FCSTD DOCUMENT  (FreeCAD 0.18.4R)
Label: Abanico
License: All rights reserved
LicenseURL: http://en.wikipedia.org/wiki/All_rights_reserved
objects: Part::Part2DObjectPython×70, App::DocumentObjectGroup×1
note: 70 computed .brp shape members not serialized (recipe doc carries the construction recipe); baked Part::Feature solids carry a one-line shape summary decoded from their .brp

FEATURE [Part::Part2DObjectPython] Line  # Draft 2D object (typed FeaturePython)
  ChamferSize = 0
  Closed = true
  End = (47,0,0)
  FilletRadius = 0
  Length = 47
  MakeFace = false
  Points = (2) [(0,0,0),(47,0,0)]
  Start = (0,0,0)
  Subdivisions = 0
FEATURE [Part::Part2DObjectPython] Line001  # Draft 2D object (typed FeaturePython)
  ChamferSize = 0
  Closed = true
  End = (47,7.52818,0)
  FilletRadius = 0
  Length = 15.0564
  MakeFace = false
  Placement = pos=(47,-7.52818,0) rot=(0,0,1;0rad)
  Points = (2) [(0,0,0),(0,15.0564,0)]
  Start = (47,-7.52818,0)
  Subdivisions = 0
FEATURE [Part::Part2DObjectPython] Wire  # Draft 2D object (typed FeaturePython)
  ChamferSize = 0
  Closed = true
  End = (21.85,-0.95,0)
  FilletRadius = 0
  Length = 11.2
  MakeFace = false
  Placement = pos=(21.85,0.95,0) rot=(0,0,1;0rad)
  Points = (4) [(0,0,0),(-3.7,0,0),(-3.7,-1.9,0),(0,-1.9,0)]
  Start = (21.85,0.95,0)
  Subdivisions = 0
FEATURE [Part::Part2DObjectPython] Line002  # Draft 2D object (typed FeaturePython)
  ChamferSize = 0
  Closed = true
  End = (34.0926,32.3527,0)
  FilletRadius = 0
  Length = 47
  MakeFace = false
  Points = (2) [(0,0,0),(34.0926,32.3527,0)]
  Start = (0,0,0)
  Subdivisions = 0
FEATURE [Part::Part2DObjectPython] Line003  # Draft 2D object (typed FeaturePython)
  ChamferSize = 0
  Closed = true
  End = (28.9105,37.8134,0)
  FilletRadius = 0
  Length = 15.0564
  MakeFace = false
  Placement = pos=(39.2747,26.8919,0) rot=(0,0,1;0rad)
  Points = (2) [(0,0,0),(-10.3641,10.9215,0)]
  Start = (39.2747,26.8919,0)
  Subdivisions = 0
FEATURE [Part::Part2DObjectPython] Wire001  # Draft 2D object (typed FeaturePython)
  ChamferSize = 0
  Closed = true
  End = (16.5034,14.3514,0)
  FilletRadius = 0
  Length = 11.2
  MakeFace = false
  Placement = pos=(15.1955,15.7297,0) rot=(0,0,1;0rad)
  Points = (4) [(0,0,0),(-2.68389,-2.54691,0),(-1.37601,-3.92512,0),(1.30787,-1.37821,0)]
  Start = (15.1955,15.7297,0)
  Subdivisions = 0
FEATURE [Part::Part2DObjectPython] Circle  # Draft 2D object (typed FeaturePython)
  FirstAngle = 0
  LastAngle = 0
  MakeFace = false
  Placement = pos=(23.0803,30.1878,0) rot=(0,0,1;0rad)
  Radius = 1.6
FEATURE [Part::Part2DObjectPython] Line004  # Draft 2D object (typed FeaturePython)
  ChamferSize = 0
  Closed = true
  End = (22.2821,41.3824,0)
  FilletRadius = 0
  Length = 47
  MakeFace = false
  Points = (2) [(0,0,0),(22.2821,41.3824,0)]
  Start = (0,0,0)
  Subdivisions = 0
FEATURE [Part::Part2DObjectPython] Line005  # Draft 2D object (typed FeaturePython)
  ChamferSize = 0
  Closed = true
  End = (15.6538,44.9515,0)
  FilletRadius = 0
  Length = 15.0564
  MakeFace = false
  Placement = pos=(28.9105,37.8134,0) rot=(0,0,1;0rad)
  Points = (2) [(0,0,0),(-13.2568,7.13804,0)]
  Start = (28.9105,37.8134,0)
  Subdivisions = 0
FEATURE [Part::Part2DObjectPython] Wire002  # Draft 2D object (typed FeaturePython)
  ChamferSize = 0
  Closed = true
  End = (11.1953,18.788,0)
  FilletRadius = 0
  Length = 11.2
  MakeFace = false
  Placement = pos=(9.52237,19.6888,0) rot=(0,0,1;0rad)
  Points = (4) [(0,0,0),(-1.75413,-3.25777,0),(-0.0812194,-4.15853,0),(1.67291,-0.900768,0)]
  Start = (9.52237,19.6888,0)
  Subdivisions = 0
FEATURE [Part::Part2DObjectPython] Circle001  # Draft 2D object (typed FeaturePython)
  FirstAngle = 0
  LastAngle = 0
  MakeFace = false
  Placement = pos=(12.4969,35.8863,0) rot=(0,0,1;0rad)
  Radius = 1.6
FEATURE [Part::Part2DObjectPython] Line006  # Draft 2D object (typed FeaturePython)
  ChamferSize = 0
  Closed = true
  End = (8.24224,46.2716,0)
  FilletRadius = 0
  Length = 47
  MakeFace = false
  Points = (2) [(0,0,0),(8.24224,46.2716,0)]
  Start = (0,0,0)
  Subdivisions = 0
FEATURE [Part::Part2DObjectPython] Line007  # Draft 2D object (typed FeaturePython)
  ChamferSize = 0
  Closed = true
  End = (0.830719,47.5918,0)
  FilletRadius = 0
  Length = 15.0564
  MakeFace = false
  Placement = pos=(15.6538,44.9515,0) rot=(0,0,1;0rad)
  Points = (2) [(0,0,0),(-14.823,2.64038,0)]
  Start = (15.6538,44.9515,0)
  Subdivisions = 0
FEATURE [Part::Part2DObjectPython] Wire003  # Draft 2D object (typed FeaturePython)
  ChamferSize = 0
  Closed = true
  End = (4.76704,21.3448,0)
  FilletRadius = 0
  Length = 11.2
  MakeFace = false
  Placement = pos=(2.89648,21.678,0) rot=(0,0,1;0rad)
  Points = (4) [(0,0,0),(-0.648857,-3.64266,0),(1.2217,-3.97586,0),(1.87056,-0.333197,0)]
  Start = (2.89648,21.678,0)
  Subdivisions = 0
FEATURE [Part::Part2DObjectPython] Circle002  # Draft 2D object (typed FeaturePython)
  FirstAngle = 0
  LastAngle = 0
  MakeFace = false
  Placement = pos=(0.663191,37.9942,0) rot=(0,0,1;0rad)
  Radius = 1.6
FEATURE [Part::Part2DObjectPython] Line008  # Draft 2D object (typed FeaturePython)
  ChamferSize = 0
  Closed = true
  End = (-6.62236,46.5311,0)
  FilletRadius = 0
  Length = 47
  MakeFace = false
  Points = (2) [(0,0,0),(-6.62236,46.5311,0)]
  Start = (0,0,0)
  Subdivisions = 0
FEATURE [Part::Part2DObjectPython] Line009  # Draft 2D object (typed FeaturePython)
  ChamferSize = 0
  Closed = true
  End = (-14.0754,45.4704,0)
  FilletRadius = 0
  Length = 15.0564
  MakeFace = false
  Placement = pos=(0.830719,47.5918,0) rot=(0,0,1;0rad)
  Points = (2) [(0,0,0),(-14.9062,-2.12146,0)]
  Start = (0.830719,47.5918,0)
  Subdivisions = 0
FEATURE [Part::Part2DObjectPython] Wire004  # Draft 2D object (typed FeaturePython)
  ChamferSize = 0
  Closed = true
  End = (-2.13817,21.7659,0)
  FilletRadius = 0
  Length = 11.2
  MakeFace = false
  Placement = pos=(-4.01921,21.4982,0) rot=(0,0,1;0rad)
  Points = (4) [(0,0,0),(0.521335,-3.66309,0),(2.40238,-3.39538,0),(1.88104,0.267712,0)]
  Start = (-4.01921,21.4982,0)
  Subdivisions = 0
FEATURE [Part::Part2DObjectPython] Circle003  # Draft 2D object (typed FeaturePython)
  FirstAngle = 0
  LastAngle = 0
  MakeFace = false
  Placement = pos=(-11.2369,36.3006,0) rot=(0,0,1;0rad)
  Radius = 1.6
FEATURE [Part::Part2DObjectPython] Line010  # Draft 2D object (typed FeaturePython)
  ChamferSize = 0
  Closed = true
  End = (-20.8243,42.1349,0)
  FilletRadius = 0
  Length = 47
  MakeFace = false
  Points = (2) [(0,0,0),(-20.8243,42.1349,0)]
  Start = (0,0,0)
  Subdivisions = 0
FEATURE [Part::Part2DObjectPython] Line011  # Draft 2D object (typed FeaturePython)
  ChamferSize = 0
  Closed = true
  End = (-27.5733,38.7993,0)
  FilletRadius = 0
  Length = 15.0564
  MakeFace = false
  Placement = pos=(-14.0754,45.4704,0) rot=(0,0,1;0rad)
  Points = (2) [(0,0,0),(-13.4978,-6.67104,0)]
  Start = (-14.0754,45.4704,0)
  Subdivisions = 0
FEATURE [Part::Part2DObjectPython] Wire005  # Draft 2D object (typed FeaturePython)
  ChamferSize = 0
  Closed = true
  End = (-8.82944,20.0091,0)
  FilletRadius = 0
  Length = 11.2
  MakeFace = false
  Placement = pos=(-10.5328,19.1673,0) rot=(0,0,1;0rad)
  Points = (4) [(0,0,0),(1.63936,-3.317,0),(3.34269,-2.47516,0),(1.70332,0.841835,0)]
  Start = (-10.5328,19.1673,0)
  Subdivisions = 0
FEATURE [Part::Part2DObjectPython] Circle004  # Draft 2D object (typed FeaturePython)
  FirstAngle = 0
  LastAngle = 0
  MakeFace = false
  Placement = pos=(-22.0127,30.9749,0) rot=(0,0,1;0rad)
  Radius = 1.6
FEATURE [Part::Part2DObjectPython] Line012  # Draft 2D object (typed FeaturePython)
  ChamferSize = 0
  Closed = true
  End = (-32.9427,33.5228,0)
  FilletRadius = 0
  Length = 47
  MakeFace = false
  Points = (2) [(0,0,0),(-32.9427,33.5228,0)]
  Start = (0,0,0)
  Subdivisions = 0
FEATURE [Part::Part2DObjectPython] Line013  # Draft 2D object (typed FeaturePython)
  ChamferSize = 0
  Closed = true
  End = (-38.3122,28.2462,0)
  FilletRadius = 0
  Length = 15.0564
  MakeFace = false
  Placement = pos=(-27.5733,38.7993,0) rot=(0,0,1;0rad)
  Points = (2) [(0,0,0),(-10.739,-10.5531,0)]
  Start = (-27.5733,38.7993,0)
  Subdivisions = 0
FEATURE [Part::Part2DObjectPython] Wire006  # Draft 2D object (typed FeaturePython)
  ChamferSize = 0
  Closed = true
  End = (-14.6373,16.2504,0)
  FilletRadius = 0
  Length = 11.2
  MakeFace = false
  Placement = pos=(-15.9925,14.9187,0) rot=(0,0,1;0rad)
  Points = (4) [(0,0,0),(2.59336,-2.63903,0),(3.94854,-1.3073,0),(1.35518,1.33173,0)]
  Start = (-15.9925,14.9187,0)
  Subdivisions = 0
FEATURE [Part::Part2DObjectPython] Circle005  # Draft 2D object (typed FeaturePython)
  FirstAngle = 0
  LastAngle = 0
  MakeFace = false
  Placement = pos=(-30.586,22.5499,0) rot=(0,0,1;0rad)
  Radius = 1.6
FEATURE [Part::Part2DObjectPython] Line014  # Draft 2D object (typed FeaturePython)
  ChamferSize = 0
  Closed = true
  End = (-41.765,21.5565,0)
  FilletRadius = 0
  Length = 47
  MakeFace = false
  Points = (2) [(0,0,0),(-41.765,21.5565,0)]
  Start = (0,0,0)
  Subdivisions = 0
FEATURE [Part::Part2DObjectPython] Line015  # Draft 2D object (typed FeaturePython)
  ChamferSize = 0
  Closed = true
  End = (-45.2178,14.8669,0)
  FilletRadius = 0
  Length = 15.0564
  MakeFace = false
  Placement = pos=(-38.3122,28.2462,0) rot=(0,0,1;0rad)
  Points = (2) [(0,0,0),(-6.90559,-13.3793,0)]
  Start = (-38.3122,28.2462,0)
  Subdivisions = 0
FEATURE [Part::Part2DObjectPython] Wire007  # Draft 2D object (typed FeaturePython)
  ChamferSize = 0
  Closed = true
  End = (-18.9806,10.8657,0)
  FilletRadius = 0
  Length = 11.2
  MakeFace = false
  Placement = pos=(-19.852,9.17731,0) rot=(0,0,1;0rad)
  Points = (4) [(0,0,0),(3.28788,-1.697,0),(4.15932,-0.00863061,0),(0.871434,1.68837,0)]
  Start = (-19.852,9.17731,0)
  Subdivisions = 0
FEATURE [Part::Part2DObjectPython] Circle006  # Draft 2D object (typed FeaturePython)
  FirstAngle = 0
  LastAngle = 0
  MakeFace = false
  Placement = pos=(-36.0989,11.8687,0) rot=(0,0,1;0rad)
  Radius = 1.6
FEATURE [Part::Part2DObjectPython] Line016  # Draft 2D object (typed FeaturePython)
  ChamferSize = 0
  Closed = true
  End = (-46.4084,7.43343,0)
  FilletRadius = 0
  Length = 47
  MakeFace = false
  Points = (2) [(0,0,0),(-46.4084,7.43343,0)]
  Start = (0,0,0)
  Subdivisions = 0
FEATURE [Part::Part2DObjectPython] Line017  # Draft 2D object (typed FeaturePython)
  ChamferSize = 0
  Closed = true
  End = (-47.5991,1.8e-15,0)
  FilletRadius = 0
  Length = 15.0564
  MakeFace = false
  Placement = pos=(-45.2178,14.8669,0) rot=(0,0,1;0rad)
  Points = (2) [(0,0,0),(-2.38128,-14.8669,0)]
  Start = (-45.2178,14.8669,0)
  Subdivisions = 0
FEATURE [Part::Part2DObjectPython] Wire008  # Draft 2D object (typed FeaturePython)
  ChamferSize = 0
  Closed = true
  End = (-21.4247,4.3938,0)
  FilletRadius = 0
  Length = 11.2
  MakeFace = false
  Placement = pos=(-21.7252,2.51771,0) rot=(0,0,1;0rad)
  Points = (4) [(0,0,0),(3.65343,-0.585185,0),(3.95393,1.2909,0),(0.3005,1.87609,0)]
  Start = (-21.7252,2.51771,0)
  Subdivisions = 0
FEATURE [Part::Part2DObjectPython] Circle007  # Draft 2D object (typed FeaturePython)
  FirstAngle = 0
  LastAngle = 0
  MakeFace = false
  Placement = pos=(-38,4.7e-15,0) rot=(0,0,1;0rad)
  Radius = 1.6
FEATURE [Part::Part2DObjectPython] Line018  # Draft 2D object (typed FeaturePython)
  ChamferSize = 0
  Closed = true
  End = (-46.4084,-7.43343,0)
  FilletRadius = 0
  Length = 47
  MakeFace = false
  Points = (2) [(0,0,0),(-46.4084,-7.43343,0)]
  Start = (0,0,0)
  Subdivisions = 0
FEATURE [Part::Part2DObjectPython] Line019  # Draft 2D object (typed FeaturePython)
  ChamferSize = 0
  Closed = true
  End = (-45.2178,-14.8669,0)
  FilletRadius = 0
  Length = 15.0564
  MakeFace = false
  Placement = pos=(-47.5991,1.15e-14,0) rot=(0,0,1;0rad)
  Points = (2) [(0,0,0),(2.38128,-14.8669,0)]
  Start = (-47.5991,1.15e-14,0)
  Subdivisions = 0
FEATURE [Part::Part2DObjectPython] Wire009  # Draft 2D object (typed FeaturePython)
  ChamferSize = 0
  Closed = true
  End = (-21.7252,-2.51771,0)
  FilletRadius = 0
  Length = 11.2
  MakeFace = false
  Placement = pos=(-21.4247,-4.3938,0) rot=(0,0,1;0rad)
  Points = (4) [(0,0,0),(3.65343,0.585185,0),(3.35293,2.46127,0),(-0.3005,1.87609,0)]
  Start = (-21.4247,-4.3938,0)
  Subdivisions = 0
FEATURE [Part::Part2DObjectPython] Circle008  # Draft 2D object (typed FeaturePython)
  FirstAngle = 0
  LastAngle = 0
  MakeFace = false
  Placement = pos=(-36.0989,-11.8687,0) rot=(0,0,1;0rad)
  Radius = 1.6
FEATURE [Part::Part2DObjectPython] Line020  # Draft 2D object (typed FeaturePython)
  ChamferSize = 0
  Closed = true
  End = (-41.765,-21.5565,0)
  FilletRadius = 0
  Length = 47
  MakeFace = false
  Points = (2) [(0,0,0),(-41.765,-21.5565,0)]
  Start = (0,0,0)
  Subdivisions = 0
FEATURE [Part::Part2DObjectPython] Line021  # Draft 2D object (typed FeaturePython)
  ChamferSize = 0
  Closed = true
  End = (-38.3122,-28.2462,0)
  FilletRadius = 0
  Length = 15.0564
  MakeFace = false
  Placement = pos=(-45.2178,-14.8669,0) rot=(0,0,1;0rad)
  Points = (2) [(0,0,0),(6.90559,-13.3793,0)]
  Start = (-45.2178,-14.8669,0)
  Subdivisions = 0
FEATURE [Part::Part2DObjectPython] Wire010  # Draft 2D object (typed FeaturePython)
  ChamferSize = 0
  Closed = true
  End = (-19.852,-9.17731,0)
  FilletRadius = 0
  Length = 11.2
  MakeFace = false
  Placement = pos=(-18.9806,-10.8657,0) rot=(0,0,1;0rad)
  Points = (4) [(0,0,0),(3.28788,1.697,0),(2.41645,3.38538,0),(-0.871434,1.68837,0)]
  Start = (-18.9806,-10.8657,0)
  Subdivisions = 0
FEATURE [Part::Part2DObjectPython] Circle009  # Draft 2D object (typed FeaturePython)
  FirstAngle = 0
  LastAngle = 0
  MakeFace = false
  Placement = pos=(-30.586,-22.5499,0) rot=(0,0,1;0rad)
  Radius = 1.6
FEATURE [Part::Part2DObjectPython] Line022  # Draft 2D object (typed FeaturePython)
  ChamferSize = 0
  Closed = true
  End = (-32.9427,-33.5228,0)
  FilletRadius = 0
  Length = 47
  MakeFace = false
  Points = (2) [(0,0,0),(-32.9427,-33.5228,0)]
  Start = (0,0,0)
  Subdivisions = 0
FEATURE [Part::Part2DObjectPython] Line023  # Draft 2D object (typed FeaturePython)
  ChamferSize = 0
  Closed = true
  End = (-27.5733,-38.7993,0)
  FilletRadius = 0
  Length = 15.0564
  MakeFace = false
  Placement = pos=(-38.3122,-28.2462,0) rot=(0,0,1;0rad)
  Points = (2) [(0,0,0),(10.739,-10.5531,0)]
  Start = (-38.3122,-28.2462,0)
  Subdivisions = 0
FEATURE [Part::Part2DObjectPython] Wire011  # Draft 2D object (typed FeaturePython)
  ChamferSize = 0
  Closed = true
  End = (-15.9925,-14.9187,0)
  FilletRadius = 0
  Length = 11.2
  MakeFace = false
  Placement = pos=(-14.6373,-16.2504,0) rot=(0,0,1;0rad)
  Points = (4) [(0,0,0),(2.59336,2.63903,0),(1.23819,3.97075,0),(-1.35518,1.33173,0)]
  Start = (-14.6373,-16.2504,0)
  Subdivisions = 0
FEATURE [Part::Part2DObjectPython] Circle010  # Draft 2D object (typed FeaturePython)
  FirstAngle = 0
  LastAngle = 0
  MakeFace = false
  Placement = pos=(-22.0127,-30.9749,0) rot=(0,0,1;0rad)
  Radius = 1.6
FEATURE [Part::Part2DObjectPython] Line024  # Draft 2D object (typed FeaturePython)
  ChamferSize = 0
  Closed = true
  End = (-20.8243,-42.1349,0)
  FilletRadius = 0
  Length = 47
  MakeFace = false
  Points = (2) [(0,0,0),(-20.8243,-42.1349,0)]
  Start = (0,0,0)
  Subdivisions = 0
FEATURE [Part::Part2DObjectPython] Line025  # Draft 2D object (typed FeaturePython)
  ChamferSize = 0
  Closed = true
  End = (-14.0754,-45.4704,0)
  FilletRadius = 0
  Length = 15.0564
  MakeFace = false
  Placement = pos=(-27.5733,-38.7993,0) rot=(0,0,1;0rad)
  Points = (2) [(0,0,0),(13.4978,-6.67104,0)]
  Start = (-27.5733,-38.7993,0)
  Subdivisions = 0
FEATURE [Part::Part2DObjectPython] Wire012  # Draft 2D object (typed FeaturePython)
  ChamferSize = 0
  Closed = true
  End = (-10.5328,-19.1673,0)
  FilletRadius = 0
  Length = 11.2
  MakeFace = false
  Placement = pos=(-8.82944,-20.0091,0) rot=(0,0,1;0rad)
  Points = (4) [(0,0,0),(1.63936,3.317,0),(-0.0639608,4.15884,0),(-1.70332,0.841835,0)]
  Start = (-8.82944,-20.0091,0)
  Subdivisions = 0
FEATURE [Part::Part2DObjectPython] Circle011  # Draft 2D object (typed FeaturePython)
  FirstAngle = 0
  LastAngle = 0
  MakeFace = false
  Placement = pos=(-11.2369,-36.3006,0) rot=(0,0,1;0rad)
  Radius = 1.6
FEATURE [Part::Part2DObjectPython] Line026  # Draft 2D object (typed FeaturePython)
  ChamferSize = 0
  Closed = true
  End = (-6.62236,-46.5311,0)
  FilletRadius = 0
  Length = 47
  MakeFace = false
  Points = (2) [(0,0,0),(-6.62236,-46.5311,0)]
  Start = (0,0,0)
  Subdivisions = 0
FEATURE [Part::Part2DObjectPython] Line027  # Draft 2D object (typed FeaturePython)
  ChamferSize = 0
  Closed = true
  End = (0.830719,-47.5918,0)
  FilletRadius = 0
  Length = 15.0564
  MakeFace = false
  Placement = pos=(-14.0754,-45.4704,0) rot=(0,0,1;0rad)
  Points = (2) [(0,0,0),(14.9062,-2.12146,0)]
  Start = (-14.0754,-45.4704,0)
  Subdivisions = 0
FEATURE [Part::Part2DObjectPython] Wire013  # Draft 2D object (typed FeaturePython)
  ChamferSize = 0
  Closed = true
  End = (-4.01921,-21.4982,0)
  FilletRadius = 0
  Length = 11.2
  MakeFace = false
  Placement = pos=(-2.13817,-21.7659,0) rot=(0,0,1;0rad)
  Points = (4) [(0,0,0),(0.521335,3.66309,0),(-1.35971,3.9308,0),(-1.88104,0.267712,0)]
  Start = (-2.13817,-21.7659,0)
  Subdivisions = 0
FEATURE [Part::Part2DObjectPython] Circle012  # Draft 2D object (typed FeaturePython)
  FirstAngle = 0
  LastAngle = 0
  MakeFace = false
  Placement = pos=(0.663191,-37.9942,0) rot=(0,0,1;0rad)
  Radius = 1.6
FEATURE [Part::Part2DObjectPython] Line028  # Draft 2D object (typed FeaturePython)
  ChamferSize = 0
  Closed = true
  End = (8.24224,-46.2716,0)
  FilletRadius = 0
  Length = 47
  MakeFace = false
  Points = (2) [(0,0,0),(8.24224,-46.2716,0)]
  Start = (0,0,0)
  Subdivisions = 0
FEATURE [Part::Part2DObjectPython] Line029  # Draft 2D object (typed FeaturePython)
  ChamferSize = 0
  Closed = true
  End = (15.6538,-44.9515,0)
  FilletRadius = 0
  Length = 15.0564
  MakeFace = false
  Placement = pos=(0.830719,-47.5918,0) rot=(0,0,1;0rad)
  Points = (2) [(0,0,0),(14.823,2.64038,0)]
  Start = (0.830719,-47.5918,0)
  Subdivisions = 0
FEATURE [Part::Part2DObjectPython] Wire014  # Draft 2D object (typed FeaturePython)
  ChamferSize = 0
  Closed = true
  End = (2.89648,-21.678,0)
  FilletRadius = 0
  Length = 11.2
  MakeFace = false
  Placement = pos=(4.76704,-21.3448,0) rot=(0,0,1;0rad)
  Points = (4) [(0,0,0),(-0.648857,3.64266,0),(-2.51941,3.30946,0),(-1.87056,-0.333197,0)]
  Start = (4.76704,-21.3448,0)
  Subdivisions = 0
FEATURE [Part::Part2DObjectPython] Circle013  # Draft 2D object (typed FeaturePython)
  FirstAngle = 0
  LastAngle = 0
  MakeFace = false
  Placement = pos=(12.4969,-35.8863,0) rot=(0,0,1;0rad)
  Radius = 1.6
FEATURE [Part::Part2DObjectPython] Line030  # Draft 2D object (typed FeaturePython)
  ChamferSize = 0
  Closed = true
  End = (22.2821,-41.3824,0)
  FilletRadius = 0
  Length = 47
  MakeFace = false
  Points = (2) [(0,0,0),(22.2821,-41.3824,0)]
  Start = (0,0,0)
  Subdivisions = 0
FEATURE [Part::Part2DObjectPython] Line031  # Draft 2D object (typed FeaturePython)
  ChamferSize = 0
  Closed = true
  End = (28.9105,-37.8134,0)
  FilletRadius = 0
  Length = 15.0564
  MakeFace = false
  Placement = pos=(15.6538,-44.9515,0) rot=(0,0,1;0rad)
  Points = (2) [(0,0,0),(13.2568,7.13804,0)]
  Start = (15.6538,-44.9515,0)
  Subdivisions = 0
FEATURE [Part::Part2DObjectPython] Wire015  # Draft 2D object (typed FeaturePython)
  ChamferSize = 0
  Closed = true
  End = (9.52237,-19.6888,0)
  FilletRadius = 0
  Length = 11.2
  MakeFace = false
  Placement = pos=(11.1953,-18.788,0) rot=(0,0,1;0rad)
  Points = (4) [(0,0,0),(-1.75413,3.25777,0),(-3.42703,2.357,0),(-1.67291,-0.900768,0)]
  Start = (11.1953,-18.788,0)
  Subdivisions = 0
FEATURE [Part::Part2DObjectPython] Circle014  # Draft 2D object (typed FeaturePython)
  FirstAngle = 0
  LastAngle = 0
  MakeFace = false
  Placement = pos=(23.0803,-30.1878,0) rot=(0,0,1;0rad)
  Radius = 1.6
FEATURE [Part::Part2DObjectPython] Line032  # Draft 2D object (typed FeaturePython)
  ChamferSize = 0
  Closed = true
  End = (34.0926,-32.3527,0)
  FilletRadius = 0
  Length = 47
  MakeFace = false
  Points = (2) [(0,0,0),(34.0926,-32.3527,0)]
  Start = (0,0,0)
  Subdivisions = 0
FEATURE [Part::Part2DObjectPython] Line033  # Draft 2D object (typed FeaturePython)
  ChamferSize = 0
  Closed = true
  End = (39.2747,-26.8919,0)
  FilletRadius = 0
  Length = 15.0564
  MakeFace = false
  Placement = pos=(28.9105,-37.8134,0) rot=(0,0,1;0rad)
  Points = (2) [(0,0,0),(10.3641,10.9215,0)]
  Start = (28.9105,-37.8134,0)
  Subdivisions = 0
FEATURE [Part::Part2DObjectPython] Wire016  # Draft 2D object (typed FeaturePython)
  ChamferSize = 0
  Closed = true
  End = (15.1955,-15.7297,0)
  FilletRadius = 0
  Length = 11.2
  MakeFace = false
  Placement = pos=(16.5034,-14.3514,0) rot=(0,0,1;0rad)
  Points = (4) [(0,0,0),(-2.68389,2.54691,0),(-3.99176,1.1687,0),(-1.30787,-1.37821,0)]
  Start = (16.5034,-14.3514,0)
  Subdivisions = 0
FEATURE [Part::Part2DObjectPython] Circle015  # Draft 2D object (typed FeaturePython)
  FirstAngle = 0
  LastAngle = 0
  MakeFace = false
  Placement = pos=(35.2948,14.0812,0) rot=(0,0,1;0rad)
  Radius = 1.6
FEATURE [Part::Part2DObjectPython] Circle016  # Draft 2D object (typed FeaturePython)
  FirstAngle = 0
  LastAngle = 0
  MakeFace = false
  Placement = pos=(35.2948,-14.0812,0) rot=(0,0,1;0rad)
  Radius = 1.6
FEATURE [Part::Part2DObjectPython] Line034  # Draft 2D object (typed FeaturePython)
  ChamferSize = 0
  Closed = false
  End = (47,7.52818,0)
  FilletRadius = 0
  Length = 20.8479
  MakeFace = false
  Placement = pos=(39.2747,26.8919,0) rot=(0,0,1;0rad)
  Points = (2) [(0,0,0),(7.72535,-19.3637,0)]
  Start = (39.2747,26.8919,0)
  Subdivisions = 0
FEATURE [Part::Part2DObjectPython] Line035  # Draft 2D object (typed FeaturePython)
  ChamferSize = 0
  Closed = false
  End = (39.2747,-26.8919,0)
  FilletRadius = 0
  Length = 20.8479
  MakeFace = false
  Placement = pos=(47,-7.52818,0) rot=(0,0,1;0rad)
  Points = (2) [(0,0,0),(-7.72535,-19.3637,0)]
  Start = (47,-7.52818,0)
  Subdivisions = 0
FEATURE [App::DocumentObjectGroup] Group  label="Borders"
  Group = -> [Line034,Line003,Line005,Line007,Line009,Line011,Line013,Line015,Line017,Line019,Line021,Line023,Line025,Line027,Line029,Line031,Line033,Line035,Line001]
